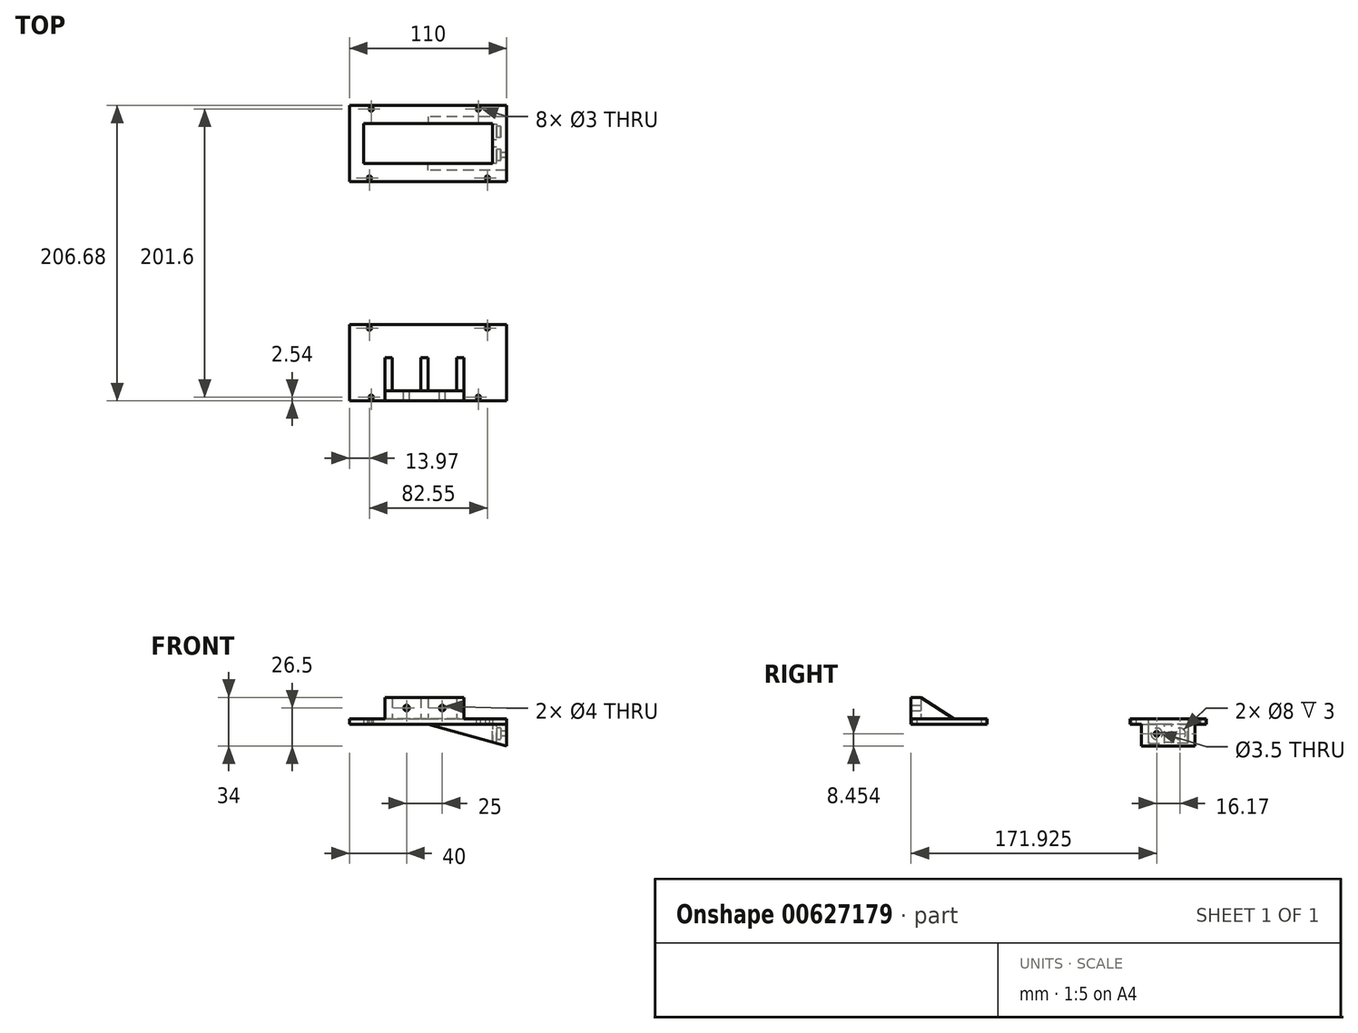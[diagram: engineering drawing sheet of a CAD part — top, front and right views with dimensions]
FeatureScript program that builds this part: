
annotation { "Feature Type Name" : "Feature", "Feature Type Description" : "" }
export const myFeature = defineFeature(function(context is Context, id is Id, definition is map)
    precondition{}
    {
        {
            var Q0;
            Q0=qCreatedBy(makeId("Top.planeOp"),FACE);
            var sketch = newSketch(context, id + "F0", { "sketchPlane" : qUnion([Q0])});
            skLineSegment(sketch, "E0.bottom", {"start": v(55, -26.67) * mm, "end": v(-55, -26.67) * mm});
            skLineSegment(sketch, "E0.top", {"start": v(55, 26.67) * mm, "end": v(-55, 26.67) * mm});
            skLineSegment(sketch, "E0.left", {"start": v(55, -26.67) * mm, "end": v(55, 26.67) * mm});
            skLineSegment(sketch, "E0.right", {"start": v(-55, -26.67) * mm, "end": v(-55, 26.67) * mm});
            skPoint(sketch, "E0.middle", {"position": v(0, 0) * mm});
            skCircle(sketch, "E1", {"center": v(-39.76, 24.13) * mm, "radius": 1.5 * mm});
            skCircle(sketch, "E2", {"center": v(35.17, 24.13) * mm, "radius": 1.5 * mm});
            skCircle(sketch, "E3", {"center": v(41.52, -24.13) * mm, "radius": 1.5 * mm});
            skCircle(sketch, "E4", {"center": v(-41.03, -24.13) * mm, "radius": 1.5 * mm});
            skLineSegment(sketch, "E5", {"start": v(-55, -76.67) * mm, "end": v(55, -76.67) * mm, "construction": true});
            skCircle(sketch, "E6.MirrorC", {"center": v(41.52, -129.21) * mm, "radius": 1.5 * mm});
            skCircle(sketch, "E7.MirrorC", {"center": v(-41.03, -129.21) * mm, "radius": 1.5 * mm});
            skCircle(sketch, "E8.MirrorC", {"center": v(-39.76, -177.47) * mm, "radius": 1.5 * mm});
            skCircle(sketch, "E9.MirrorC", {"center": v(35.17, -177.47) * mm, "radius": 1.5 * mm});
            skLineSegment(sketch, "E10.MirrorCS", {"start": v(55, -126.67) * mm, "end": v(55, -180) * mm});
            skLineSegment(sketch, "E11.MirrorCS", {"start": v(-55, -126.67) * mm, "end": v(-55, -180.01) * mm});
            skLineSegment(sketch, "E12.MirrorCS", {"start": v(55, -126.67) * mm, "end": v(-55, -126.67) * mm});
            skPoint(sketch, "E13.MirrorP", {"position": v(0, -153.34) * mm});
            skLineSegment(sketch, "E14.MirrorCS", {"start": v(55, -180) * mm, "end": v(-55, -180.01) * mm});
            skLineSegment(sketch, "E15.bottom", {"start": v(45, 14) * mm, "end": v(-45, 14) * mm});
            skLineSegment(sketch, "E15.top", {"start": v(45, -14) * mm, "end": v(-45, -14) * mm});
            skLineSegment(sketch, "E15.left", {"start": v(45, 14) * mm, "end": v(45, -14) * mm});
            skLineSegment(sketch, "E15.right", {"start": v(-45, 14) * mm, "end": v(-45, -14) * mm});
            skSolve(sketch);
        }
        {
            var Q0;
            Q0 = qSketchRegion(id + "F0", true);
            extrude(context, id + "F1", {"entities" : qUnion([Q0]), "depth" : 4 * mm, "offsetDistance" : 25 * mm});
        }
        {
            var Q0;
            Q0=makeQuery(id+"F1.opExtrude","CAP_FACE",FACE,{"disambiguationData":[OSD([sQuery(id+"F0.wireOp",EDGE,"E0.bottom"),sQuery(id+"F0.wireOp",EDGE,"E0.top"),sQuery(id+"F0.wireOp",EDGE,"E0.left"),sQuery(id+"F0.wireOp",EDGE,"E0.right"),sQuery(id+"F0.wireOp",EDGE,"E1"),sQuery(id+"F0.wireOp",EDGE,"E2"),sQuery(id+"F0.wireOp",EDGE,"E3"),sQuery(id+"F0.wireOp",EDGE,"E4")])],"isStart":true});
            var sketch = newSketch(context, id + "F2", { "sketchPlane" : qUnion([Q0])});
            skLineSegment(sketch, "E16", {"start": v(55, 18.67) * mm, "end": v(0, 18.67) * mm});
            skLineSegment(sketch, "E17", {"start": v(0, 18.67) * mm, "end": v(0, 13.67) * mm});
            skLineSegment(sketch, "E18", {"start": v(0, 13.67) * mm, "end": v(55, 13.67) * mm});
            skLineSegment(sketch, "E19", {"start": v(0, 0) * mm, "end": v(81.78, 0) * mm, "construction": true});
            skPoint(sketch, "E19.endSnap0", {"position": v(55, 0) * mm});
            skLineSegment(sketch, "E20.MirrorCS", {"start": v(0, -13.67) * mm, "end": v(55, -13.67) * mm});
            skLineSegment(sketch, "E21.MirrorCS", {"start": v(0, -18.67) * mm, "end": v(0, -13.67) * mm});
            skLineSegment(sketch, "E22.MirrorCS", {"start": v(55, -18.67) * mm, "end": v(0, -18.67) * mm});
            skLineSegment(sketch, "E23", {"start": v(55, 2.5) * mm, "end": v(0, 2.5) * mm});
            skLineSegment(sketch, "E24", {"start": v(0, 2.5) * mm, "end": v(0, 0) * mm});
            skLineSegment(sketch, "E25.MirrorCS", {"start": v(55, -2.5) * mm, "end": v(0, -2.5) * mm});
            skLineSegment(sketch, "E26.MirrorCS", {"start": v(0, -2.5) * mm, "end": v(0, 0) * mm});
            skLineSegment(sketch, "E27", {"start": v(48, 13.67) * mm, "end": v(48, 2.5) * mm});
            skLineSegment(sketch, "E28.MirrorCS", {"start": v(48, -13.67) * mm, "end": v(48, -2.5) * mm});
            skSolve(sketch);
        }
        {
            var Q0;
            Q0 = qSketchRegion(id + "F2", true);
            var Q1;
            {var subQ0=sQuery(id+"F2.wireOp",EDGE,"E16");Q1=makeQuery(id+"F2.imprint","IMPRINT",FACE,{"disambiguationData":[TD([[makeQuery(id+"F2.imprint","IMPRINT",EDGE,{"derivedFrom":subQ0}),1.0]])]});}
            var Q2;
            {var subQ1=sQuery(id+"F2.wireOp",EDGE,"E23");Q2=makeQuery(id+"F2.imprint","IMPRINT",FACE,{"disambiguationData":[TD([[makeQuery(id+"F2.imprint","IMPRINT",EDGE,{"derivedFrom":subQ1}),1.0]])]});}
            var Q3;
            {var subQ0=sQuery(id+"F2.wireOp",EDGE,"E20.MirrorCS");Q3=makeQuery(id+"F2.imprint","IMPRINT",FACE,{"disambiguationData":[TD([[makeQuery(id+"F2.imprint","IMPRINT",EDGE,{"derivedFrom":subQ0}),-1.0]])]});}
            var Q4;
            {var subQ3=sQuery(id+"F2.wireOp",EDGE,"E27");Q4=makeQuery(id+"F2.imprint","IMPRINT",FACE,{"disambiguationData":[TD([[makeQuery(id+"F2.imprint","IMPRINT",EDGE,{"derivedFrom":subQ3}),1.0]])]});}
            var Q5;
            {var subQ3=sQuery(id+"F2.wireOp",EDGE,"E28.MirrorCS");Q5=makeQuery(id+"F2.imprint","IMPRINT",FACE,{"disambiguationData":[TD([[makeQuery(id+"F2.imprint","IMPRINT",EDGE,{"derivedFrom":subQ3}),-1.0]])]});}
            extrude(context, id + "F3", {"entities" : qUnion([Q0, Q1, Q2, Q3, Q4, Q5]), "operationType" : NewBodyOperationType.ADD, "depth" : 15 * mm, "offsetDistance" : 25 * mm});
        }
        {
            var Q0;
            Q0=makeQuery(id+"F3.opExtrude","SWEPT_FACE",FACE,{"disambiguationData":[OSD([sQuery(id+"F2.wireOp",EDGE,"E16")])]});
            var sketch = newSketch(context, id + "F4", { "sketchPlane" : qUnion([Q0])});
            skLineSegment(sketch, "E29", {"start": v(0, 0) * mm, "end": v(55, -15) * mm});
            skSolve(sketch);
        }
        {
            var Q0;
            Q0 = qSketchRegion(id + "F4", true);
            var Q1;
            Q1=makeQuery(id+"F4.imprint","IMPRINT",FACE,{"disambiguationData":[TD([[makeQuery(id+"F4.imprint","IMPRINT",EDGE,{"derivedFrom":sQuery(id+"F4.wireOp",EDGE,"E29")}),-1.0]])]});
            extrude(context, id + "F5", {"entities" : qUnion([Q0, Q1]), "operationType" : NewBodyOperationType.REMOVE, "oppositeDirection" : true, "depth" : 60 * mm, "offsetDistance" : 25 * mm});
        }
        {
            var Q0;
            Q0=makeQuery(id+"F3.opExtrude","SWEPT_FACE",FACE,{"disambiguationData":[OSD([sQuery(id+"F2.wireOp",EDGE,"E27")])]});
            var sketch = newSketch(context, id + "F6", { "sketchPlane" : qUnion([Q0])});
            skCircle(sketch, "E30", {"center": v(8.09, -6.55) * mm, "radius": 1.75 * mm});
            skPoint(sketch, "E30.centerSnap0", {"position": v(13.67, -6.55) * mm});
            skPoint(sketch, "E30.centerSnap1", {"position": v(8.09, 0) * mm});
            skLineSegment(sketch, "E31", {"start": v(0, 0) * mm, "end": v(0, -17.8) * mm, "construction": true});
            skCircle(sketch, "E32.MirrorC", {"center": v(-8.09, -6.55) * mm, "radius": 1.75 * mm});
            skSolve(sketch);
        }
        {
            var Q0;
            Q0=makeQuery(id+"F6.imprint","IMPRINT",FACE,{"disambiguationData":[TD([[makeQuery(id+"F6.imprint","IMPRINT",EDGE,{"derivedFrom":sQuery(id+"F6.wireOp",EDGE,"E30")}),1.0]])]});
            var Q1;
            Q1=makeQuery(id+"F6.imprint","IMPRINT",FACE,{"disambiguationData":[TD([[makeQuery(id+"F6.imprint","IMPRINT",EDGE,{"derivedFrom":sQuery(id+"F6.wireOp",EDGE,"E32.MirrorC")}),-1.0]])]});
            extrude(context, id + "F7", {"entities" : qUnion([Q0, Q1]), "operationType" : NewBodyOperationType.REMOVE, "oppositeDirection" : true, "depth" : 8 * mm, "offsetDistance" : 25 * mm});
        }
        {
            var Q0;
            Q0=makeQuery(id+"F1.opExtrude","CAP_FACE",FACE,{"disambiguationData":[OSD([sQuery(id+"F0.wireOp",EDGE,"E6.MirrorC"),sQuery(id+"F0.wireOp",EDGE,"E7.MirrorC"),sQuery(id+"F0.wireOp",EDGE,"E8.MirrorC"),sQuery(id+"F0.wireOp",EDGE,"E9.MirrorC"),sQuery(id+"F0.wireOp",EDGE,"E10.MirrorCS"),sQuery(id+"F0.wireOp",EDGE,"E11.MirrorCS"),sQuery(id+"F0.wireOp",EDGE,"E12.MirrorCS"),sQuery(id+"F0.wireOp",EDGE,"E14.MirrorCS")])],"isStart":false});
            var sketch = newSketch(context, id + "F8", { "sketchPlane" : qUnion([Q0])});
            skLineSegment(sketch, "E33.bottom", {"start": v(-30, -180.01) * mm, "end": v(-25, -180.01) * mm});
            skLineSegment(sketch, "E33.top", {"start": v(-30, -150.01) * mm, "end": v(-25, -150.01) * mm});
            skLineSegment(sketch, "E33.left", {"start": v(-30, -180.01) * mm, "end": v(-30, -150.01) * mm});
            skLineSegment(sketch, "E33.right", {"start": v(-25, -180.01) * mm, "end": v(-25, -150.01) * mm});
            skLineSegment(sketch, "E34.bottom", {"start": v(-5, -180.01) * mm, "end": v(0, -180.01) * mm});
            skLineSegment(sketch, "E34.top", {"start": v(-5, -150.01) * mm, "end": v(0, -150.01) * mm});
            skLineSegment(sketch, "E34.left", {"start": v(-5, -180.01) * mm, "end": v(-5, -150.01) * mm});
            skLineSegment(sketch, "E34.right", {"start": v(0, -180.01) * mm, "end": v(0, -150.01) * mm});
            skLineSegment(sketch, "E35.bottom", {"start": v(20, -180.01) * mm, "end": v(25, -180.01) * mm});
            skLineSegment(sketch, "E35.top", {"start": v(20, -150.01) * mm, "end": v(25, -150.01) * mm});
            skLineSegment(sketch, "E35.left", {"start": v(20, -180.01) * mm, "end": v(20, -150.01) * mm});
            skLineSegment(sketch, "E35.right", {"start": v(25, -180.01) * mm, "end": v(25, -150.01) * mm});
            skLineSegment(sketch, "E36.bottom", {"start": v(-25, -180.01) * mm, "end": v(-5, -180.01) * mm});
            skLineSegment(sketch, "E36.top", {"start": v(-25, -173.01) * mm, "end": v(-5, -173.01) * mm});
            skLineSegment(sketch, "E36.left", {"start": v(-25, -180.01) * mm, "end": v(-25, -173.01) * mm});
            skLineSegment(sketch, "E36.right", {"start": v(-5, -180.01) * mm, "end": v(-5, -173.01) * mm});
            skLineSegment(sketch, "E37", {"start": v(0, -173.01) * mm, "end": v(20, -173.01) * mm});
            skSolve(sketch);
        }
        {
            var Q0;
            Q0 = qSketchRegion(id + "F8", true);
            var Q1;
            {var subQ3=sQuery(id+"F8.wireOp",EDGE,"E37");Q1=makeQuery(id+"F8.imprint","IMPRINT",FACE,{"disambiguationData":[TD([[makeQuery(id+"F8.imprint","IMPRINT",EDGE,{"derivedFrom":subQ3}),-1.0]])]});}
            extrude(context, id + "F9", {"entities" : qUnion([Q0, Q1]), "operationType" : NewBodyOperationType.ADD, "depth" : 15 * mm, "offsetDistance" : 25 * mm});
        }
        {
            var Q0;
            Q0=makeQuery(id+"F9.opExtrude","SWEPT_FACE",FACE,{"disambiguationData":[OSD([sQuery(id+"F8.wireOp",EDGE,"E33.right")])]});
            var sketch = newSketch(context, id + "F10", { "sketchPlane" : qUnion([Q0])});
            skLineSegment(sketch, "E38", {"start": v(-173.01, 19) * mm, "end": v(-150.01, 4) * mm});
            skSolve(sketch);
        }
        {
            var Q0;
            Q0=makeQuery(id+"F10.imprint","IMPRINT",FACE,{"disambiguationData":[TD([[makeQuery(id+"F10.imprint","IMPRINT",EDGE,{"derivedFrom":sQuery(id+"F10.wireOp",EDGE,"E38")}),1.0]])]});
            extrude(context, id + "F11", {"entities" : qUnion([Q0]), "operationType" : NewBodyOperationType.REMOVE, "depth" : 50 * mm, "offsetDistance" : 25 * mm, "hasSecondDirection" : true, "secondDirectionOppositeDirection" : true, "secondDirectionDepth" : 25 * mm});
        }
        {
            var Q0;
            Q0=makeQuery(id+"F9.opExtrude","SWEPT_FACE",FACE,{"disambiguationData":[OSD([sQuery(id+"F8.wireOp",EDGE,"E36.top")])]});
            var sketch = newSketch(context, id + "F12", { "sketchPlane" : qUnion([Q0])});
            skCircle(sketch, "E39", {"center": v(15, 11.5) * mm, "radius": 2 * mm});
            skPoint(sketch, "E39.centerSnap0", {"position": v(5, 11.5) * mm});
            skPoint(sketch, "E39.centerSnap1", {"position": v(15, 4) * mm});
            skCircle(sketch, "E40", {"center": v(-10, 11.5) * mm, "radius": 2 * mm});
            skSolve(sketch);
        }
        {
            var Q0;
            Q0 = qSketchRegion(id + "F12", true);
            extrude(context, id + "F13", {"entities" : qUnion([Q0]), "operationType" : NewBodyOperationType.REMOVE, "oppositeDirection" : true, "depth" : 25 * mm, "offsetDistance" : 25 * mm});
        }
        {
            var Q0;
            Q0=makeQuery(id+"F3.opExtrude","SWEPT_FACE",FACE,{"disambiguationData":[OSD([sQuery(id+"F2.wireOp",EDGE,"E28.MirrorCS")])]});
            var sketch = newSketch(context, id + "F14", { "sketchPlane" : qUnion([Q0])});
            skCircle(sketch, "E41", {"center": v(-8.08, -6.55) * mm, "radius": 4 * mm});
            skCircle(sketch, "E42.MirrorC", {"center": v(8.09, -6.55) * mm, "radius": 4 * mm});
            skSolve(sketch);
        }
        {
            var Q0;
            Q0 = qSketchRegion(id + "F14", true);
            extrude(context, id + "F15", {"entities" : qUnion([Q0]), "operationType" : NewBodyOperationType.REMOVE, "oppositeDirection" : true, "depth" : 3 * mm, "offsetDistance" : 25 * mm});
        }
    });
